# Revit family: 0041721
name_source: partatom
category: Lighting Fixtures
revit_build: Autodesk Revit 2017 (Build: 20190507_1515(x64)
units: mm (PartAtom-declared; Revit-internal decimal feet)

## family parameters
Cut with Voids When Loaded = No
Host = Face
Light Source = Yes
OmniClass Number = 23.80.70.00
OmniClass Title = Lighting
Part Type = Normal
Room Calculation Point = No
Round Connector Dimension = Use Diameter
Shared = No

## types (2) — shared parameters
Apparent Load = 3 VA
Assembly Code = D5020200
AssetType = Fixed
ClassificationName = Uniclass2015
ClassificationValue = EF_70_80
Color Filter = 16777215
Default Elevation = 1219 mm
Description = SylSafe Spot RA R EM3 NM DA is a miniature emergency recessed downlight with interchangeable optics for open area and escape route illumination. Non-maintained 3 hr emergency duration with NiMH rechargeable battery. Recharge period 24 hours. Self testing with DALI monitoring capability. Quick and easy installation with driver module and battery pack contained in articulated case that can pass through 40mm cutout. 160lm, 3W, IK03, IP30. Power Factor 0.45. Class II electrical construction.
Dimming Lamp Color Temperature Shift = <None>
DocumentationLiterature = http://www.sylvania-lighting.com
ElectricShockClassification = Class II
Emit Shape Visible in Rendering = No
Emit from Circle Diameter = 28 mm  [stored 0.0918635 ft]
HighRiskAreaLens_SYL = No
IfcExportAs = IfcLightFixtureType
IfcExportType = IfcLightFixtureType
ImpactProtectionIndex = IK03
IngressProtection = IP30
InputNominalFrequency = 50/60 Hz
InputVoltage = 230-240 V AC
Keynote = 16500
Lamp = LED
LampColourRenderingIndex = 75
LampColourTemperature = 6300 K
LampNominalLuminous = 160 lm
LampsType = LED
LuminousEfficacy = 53 lm/W
Manufacturer = Feilo Sylvania
ManufacturerName = Feilo Sylvania
Material_1_SYL = PC/ABS Plastic
Material_2_SYL = Aluminum
Material_3_SYL = LED
Material_4_SYL = Plastic, Transparent
ModelNumber = 0041721
NominalDepth = 50 mm  [stored 0.164042 ft]
NominalHeight = 45 mm  [stored 0.147638 ft]
NominalLength = 50 mm  [stored 0.164042 ft]
PowerConsumption = 3 W
PowerFactor = 0.45
Tilt Angle = -90.00°
Type Image = <None>
URL = http://www.sylvania-lighting.com
Voltage = 230 V
Weight = 8.0 kg
zero-valued in all types: Cost

## per-type parameters (varying)
| type | EscapeRouteLens_SYL | Model | ModelReference | Name | OpenAreaLens_SYL | Photometric Web File | TypeName |
| 0041721 SYLSAFE SPOT RA R EM3 NM DA - Open Area Lens | No | SylSafe Spot RA R EM3 NM DA - Open Area Lens | SylSafe Spot RA R EM3 NM DA - Open Area Lens | SylSafe Spot RA R EM3 NM DA - Open Area Lens | Yes | 0041721OA.ies | SylSafe Spot RA R EM3 NM DA - Open Area Lens |
| 0041721 SYLSAFE SPOT RA R EM3 NM DA - Escape Route Lens | Yes | SylSafe Spot RA R EM3 NM DA - Escape Route Lens | SylSafe Spot RA R EM3 NM DA - Escape Route Lens | SylSafe Spot RA R EM3 NM DA - Escape Route Lens | No | 0041721ER.ies | SylSafe Spot RA R EM3 NM DA - Escape Route Lens |

note: [stored X ft] marks values corroborated as IEEE doubles in the binary element streams (Revit-internal decimal feet)

## geometry (parser evidence)
native form markers: Sweep x3
no freeform markers — native parametric forms only
